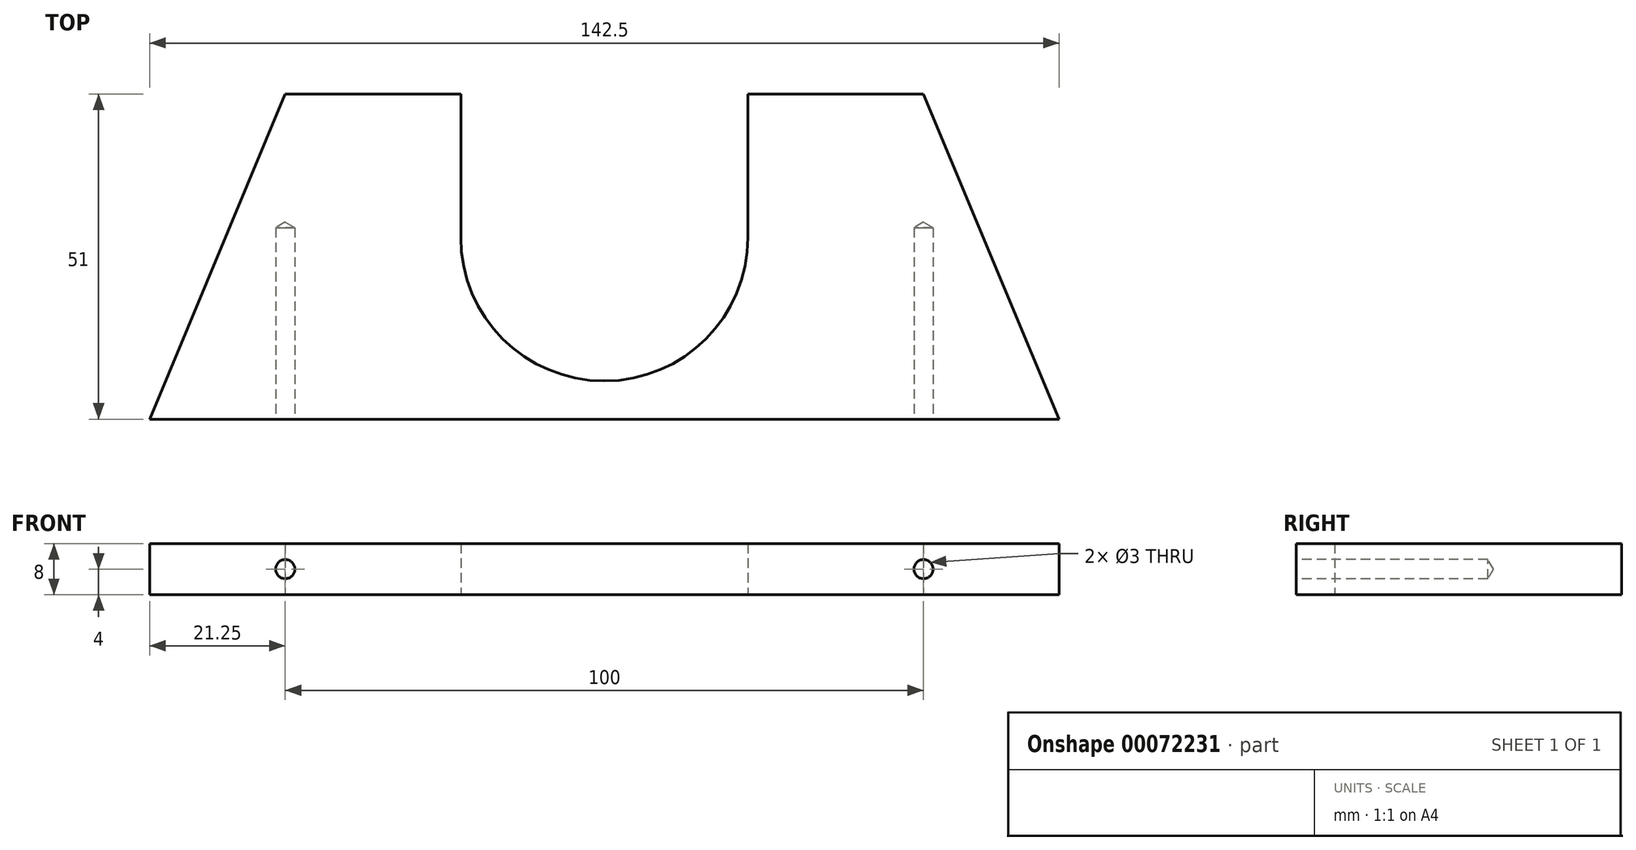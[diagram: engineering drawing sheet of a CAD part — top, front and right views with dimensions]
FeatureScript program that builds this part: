
annotation { "Feature Type Name" : "Feature", "Feature Type Description" : "" }
export const myFeature = defineFeature(function(context is Context, id is Id, definition is map)
    precondition{}
    {
        {
            var Q0;
            Q0=qCreatedBy(makeId("Top.planeOp"),FACE);
            var sketch = newSketch(context, id + "F0", { "sketchPlane" : qUnion([Q0])});
            skLineSegment(sketch, "E0.bottom", {"start": v(0, 0) * mm, "end": v(150, 0) * mm});
            skLineSegment(sketch, "E0.top", {"start": v(0, 60) * mm, "end": v(150, 60) * mm});
            skLineSegment(sketch, "E0.left", {"start": v(0, 0) * mm, "end": v(0, 60) * mm});
            skLineSegment(sketch, "E0.right", {"start": v(150, 0) * mm, "end": v(150, 60) * mm});
            skCircle(sketch, "E1", {"center": v(75, 37.5) * mm, "radius": 22.5 * mm});
            skPoint(sketch, "E2", {"position": v(75, 60) * mm});
            skLineSegment(sketch, "E3.bottom", {"start": v(75, 60) * mm, "end": v(52.5, 60) * mm});
            skLineSegment(sketch, "E3.top", {"start": v(75, 37.5) * mm, "end": v(52.5, 37.5) * mm});
            skLineSegment(sketch, "E3.left", {"start": v(75, 60) * mm, "end": v(75, 37.5) * mm});
            skLineSegment(sketch, "E3.right", {"start": v(52.5, 60) * mm, "end": v(52.5, 37.5) * mm});
            skLineSegment(sketch, "E4", {"start": v(75, 37.5) * mm, "end": v(97.5, 37.5) * mm});
            skLineSegment(sketch, "E5", {"start": v(97.5, 37.5) * mm, "end": v(97.5, 60) * mm});
            skPoint(sketch, "E6", {"position": v(25, 60) * mm});
            skPoint(sketch, "E7", {"position": v(125, 60) * mm});
            skLineSegment(sketch, "E8.bottom", {"start": v(-20, 9) * mm, "end": v(170, 9) * mm});
            skLineSegment(sketch, "E8.top", {"start": v(-20, -7) * mm, "end": v(170, -7) * mm});
            skLineSegment(sketch, "E8.left", {"start": v(-20, 9) * mm, "end": v(-20, -7) * mm});
            skLineSegment(sketch, "E8.right", {"start": v(170, 9) * mm, "end": v(170, -7) * mm});
            skPoint(sketch, "E9", {"position": v(75, -7) * mm});
            skPoint(sketch, "E10", {"position": v(75, 0) * mm});
            skLineSegment(sketch, "E11", {"start": v(125, 60) * mm, "end": v(150, 0) * mm});
            skLineSegment(sketch, "E12", {"start": v(25, 60) * mm, "end": v(0, 0) * mm});
            skSolve(sketch);
        }
        {
            var Q0;
            {var subQ5=sQuery(id+"F0.wireOp",EDGE,"E3.right");Q0=makeQuery(id+"F0.imprint","IMPRINT",FACE,{"disambiguationData":[TD([[makeQuery(id+"F0.imprint","IMPRINT",EDGE,{"derivedFrom":subQ5}),-1.0]])]});}
            extrude(context, id + "F1", {"entities" : qUnion([Q0]), "depth" : 8 * mm});
        }
        {
            var Q0;
            Q0=makeQuery(id+"F1.opExtrude","SWEPT_FACE",FACE,{"disambiguationData":[OSD([sQuery(id+"F0.wireOp",EDGE,"E8.bottom")])]});
            var sketch = newSketch(context, id + "F2", { "sketchPlane" : qUnion([Q0])});
            skLineSegment(sketch, "E13", {"start": v(3.75, 4) * mm, "end": v(3.75, 4) * mm});
            skPoint(sketch, "E14", {"position": v(25, 4) * mm});
            skPoint(sketch, "E15", {"position": v(125, 4) * mm});
            skSolve(sketch);
        }
        {
            var Q0;
            Q0=sQuery(id+"F2.wireOp",VERTEX,"E14");
            var Q1;
            Q1=sQuery(id+"F2.wireOp",VERTEX,"E15");
            var Q2;
            Q2=makeQuery(id+"F1.opExtrude","SWEPT_BODY",BODY,{"disambiguationData":[OSD([sQuery(id+"F0.wireOp",EDGE,"E0.top"),sQuery(id+"F0.wireOp",EDGE,"E0.left"),sQuery(id+"F0.wireOp",EDGE,"E0.right"),sQuery(id+"F0.wireOp",EDGE,"E1"),sQuery(id+"F0.wireOp",EDGE,"E3.right"),sQuery(id+"F0.wireOp",EDGE,"E5"),sQuery(id+"F0.wireOp",EDGE,"E8.bottom")])]});
            hole(context, id + "F3", {"style" : HoleStyle.SIMPLE, "endStyle" : HoleEndStyle.BLIND, "holeDiameter" : 3 * mm, "holeDepth" : 30 * mm, "locations" : qUnion([Q0, Q1]), "scope" : qUnion([Q2])});
        }
    });
